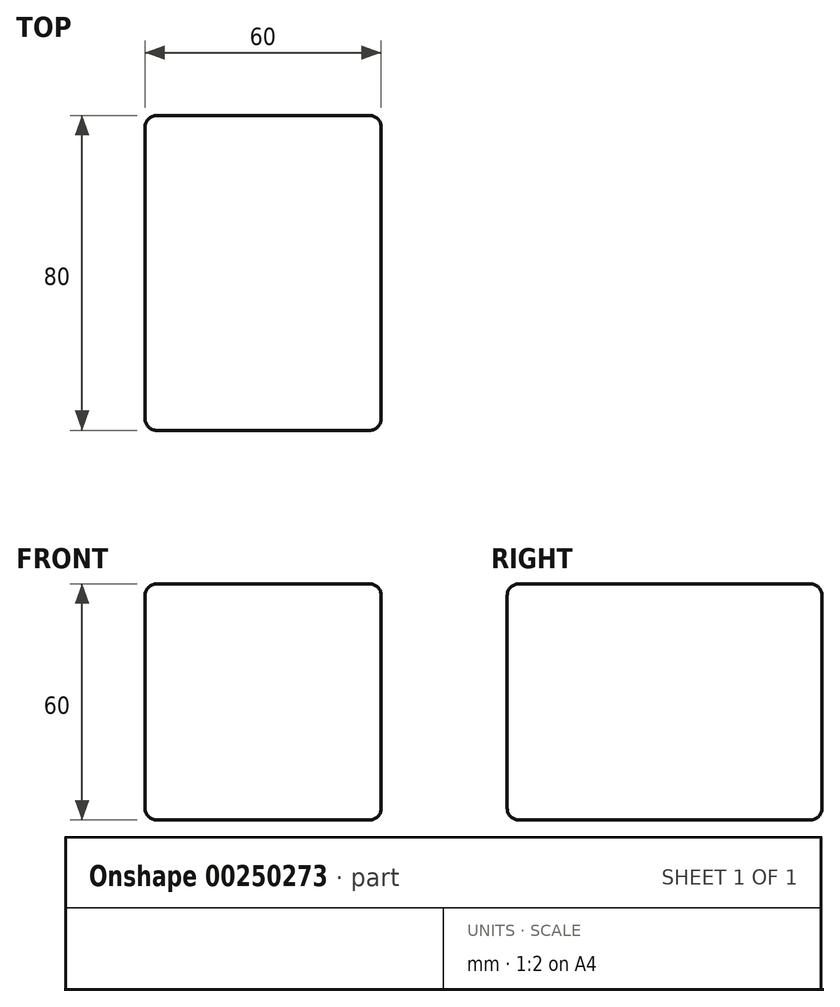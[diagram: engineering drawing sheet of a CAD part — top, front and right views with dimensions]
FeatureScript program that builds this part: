
annotation { "Feature Type Name" : "Feature", "Feature Type Description" : "" }
export const myFeature = defineFeature(function(context is Context, id is Id, definition is map)
    precondition{}
    {
        {
            var Q0;
            Q0=qCreatedBy(makeId("Top.planeOp"),FACE);
            var sketch = newSketch(context, id + "F0", { "sketchPlane" : qUnion([Q0])});
            skLineSegment(sketch, "E0", {"start": v(0, -40) * mm, "end": v(30, -40) * mm});
            skLineSegment(sketch, "E1", {"start": v(0, -40) * mm, "end": v(-30, -40) * mm});
            skLineSegment(sketch, "E2", {"start": v(30, -40) * mm, "end": v(30, 40) * mm});
            skLineSegment(sketch, "E3", {"start": v(30, 40) * mm, "end": v(-30, 40) * mm});
            skLineSegment(sketch, "E4", {"start": v(-30, 40) * mm, "end": v(-30, -40) * mm});
            skSolve(sketch);
        }
        {
            var Q0;
            Q0=makeQuery(id+"F0.imprint","IMPRINT",FACE,{"disambiguationData":[TD([[makeQuery(id+"F0.imprint","IMPRINT",EDGE,{"derivedFrom":sQuery(id+"F0.wireOp",EDGE,"E0")}),1.0]])]});
            extrude(context, id + "F1", {"entities" : qUnion([Q0]), "depth" : 60 * mm});
        }
        {
            var Q0;
            Q0=makeQuery(id+"F1.opExtrude","SWEPT_FACE",FACE,{"disambiguationData":[OSD([sQuery(id+"F0.wireOp",EDGE,"E4")])]});
            var Q1;
            Q1=makeQuery(id+"F1.opExtrude","SWEPT_FACE",FACE,{"disambiguationData":[OSD([sQuery(id+"F0.wireOp",EDGE,"E0"),sQuery(id+"F0.wireOp",EDGE,"E1")])]});
            var Q2;
            Q2=makeQuery(id+"F1.opExtrude","CAP_FACE",FACE,{"disambiguationData":[OSD([sQuery(id+"F0.wireOp",EDGE,"E0"),sQuery(id+"F0.wireOp",EDGE,"E1"),sQuery(id+"F0.wireOp",EDGE,"E2"),sQuery(id+"F0.wireOp",EDGE,"E3"),sQuery(id+"F0.wireOp",EDGE,"E4")])],"isStart":false});
            var Q3;
            Q3=makeQuery(id+"F1.opExtrude","SWEPT_FACE",FACE,{"disambiguationData":[OSD([sQuery(id+"F0.wireOp",EDGE,"E2")])]});
            var Q4;
            Q4=makeQuery(id+"F1.opExtrude","CAP_FACE",FACE,{"disambiguationData":[OSD([sQuery(id+"F0.wireOp",EDGE,"E0"),sQuery(id+"F0.wireOp",EDGE,"E1"),sQuery(id+"F0.wireOp",EDGE,"E2"),sQuery(id+"F0.wireOp",EDGE,"E3"),sQuery(id+"F0.wireOp",EDGE,"E4")])],"isStart":true});
            var Q5;
            Q5=makeQuery(id+"F1.opExtrude","SWEPT_FACE",FACE,{"disambiguationData":[OSD([sQuery(id+"F0.wireOp",EDGE,"E3")])]});
            fillet(context, id + "F2", {"entities" : qUnion([Q0, Q1, Q2, Q3, Q4, Q5]), "radius" : 3 * mm, "tangentPropagation" : true, "allowEdgeOverflow" : false});
        }
    });
